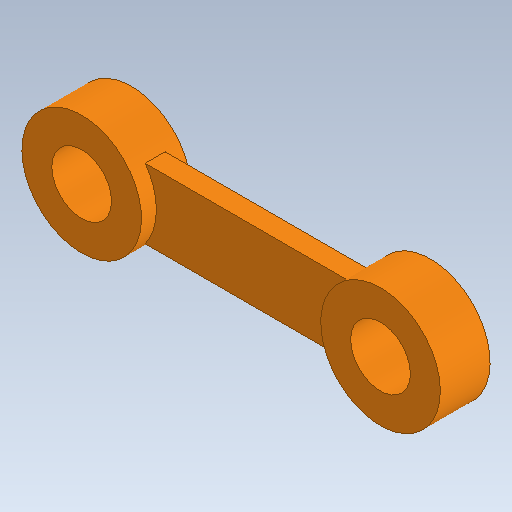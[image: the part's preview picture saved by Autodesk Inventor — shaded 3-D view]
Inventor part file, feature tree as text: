
AUTODESK INVENTOR PART (.ipt)
format: ipt  version: 2020.5 (Build 245400000, 400)  size: 121,856 bytes
history: native  units: mm
features: extrude x2, sketch x2, mirror x1
ambient origin geometry x8: Origin, YZ Plane, XZ Plane, XY Plane, X Axis, Y Axis, Z Axis, Center Point
bodies: Solid1 (feature_tree)
feature tree (5):
  extrude  "Extrusion1"  Depth=6.0mm
  extrude  "Extrusion2"  Depth=7.0mm
  mirror  "Mirror1"
  sketch  "Sketch1"  dims[d0=30.0mm d1=6.0mm]
  sketch  "Sketch2"  dims[d2=12.0mm d3=7.0mm d4=5.0mm d5=0.0mm d6=1.5mm d7=0.0mm]
